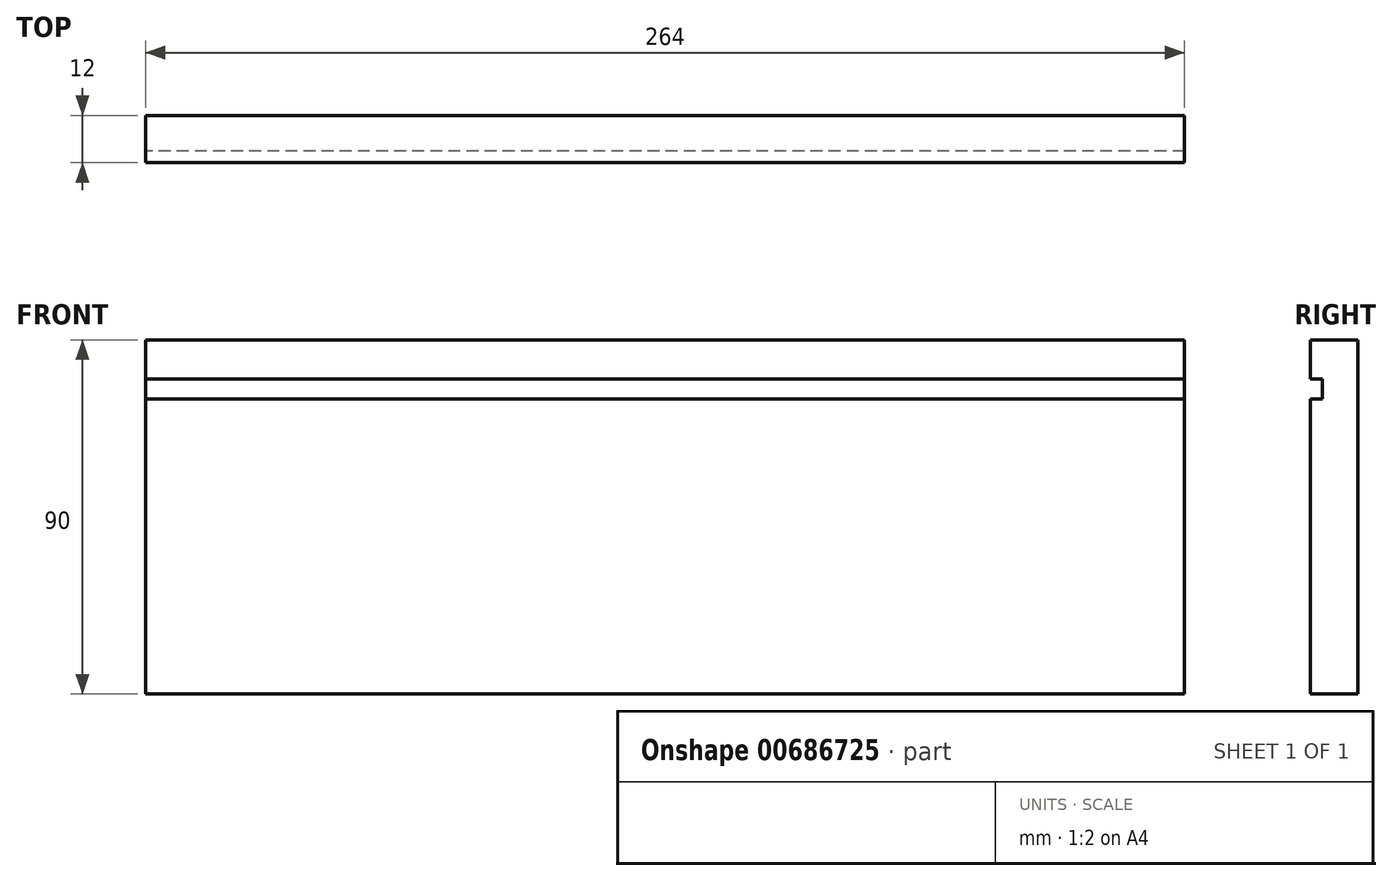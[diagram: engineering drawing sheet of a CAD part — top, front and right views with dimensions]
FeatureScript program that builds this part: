
annotation { "Feature Type Name" : "Feature", "Feature Type Description" : "" }
export const myFeature = defineFeature(function(context is Context, id is Id, definition is map)
    precondition{}
    {
        {
            var Q0;
            Q0=qCreatedBy(makeId("Right.planeOp"),FACE);
            var sketch = newSketch(context, id + "F0", { "sketchPlane" : qUnion([Q0])});
            skLineSegment(sketch, "E0.bottom", {"start": v(0, 0) * mm, "end": v(12, 0) * mm});
            skLineSegment(sketch, "E0.top", {"start": v(0, 90) * mm, "end": v(12, 90) * mm});
            skLineSegment(sketch, "E0.left", {"start": v(0, 0) * mm, "end": v(0, 75) * mm});
            skLineSegment(sketch, "E0.right", {"start": v(12, 0) * mm, "end": v(12, 90) * mm});
            skLineSegment(sketch, "E1.bottom", {"start": v(0, 80) * mm, "end": v(3, 80) * mm});
            skLineSegment(sketch, "E1.top", {"start": v(0, 75) * mm, "end": v(3, 75) * mm});
            skLineSegment(sketch, "E1.right", {"start": v(3, 80) * mm, "end": v(3, 75) * mm});
            skLineSegment(sketch, "E2.trimOffspring", {"start": v(0, 80) * mm, "end": v(0, 90) * mm});
            skSolve(sketch);
        }
        {
            var Q0;
            Q0=qSketchRegion(id+"F0",true);
            extrude(context, id + "F1", {"entities" : qUnion([Q0]), "depth" : 264 * mm, "offsetDistance" : 25 * mm});
        }
    });
